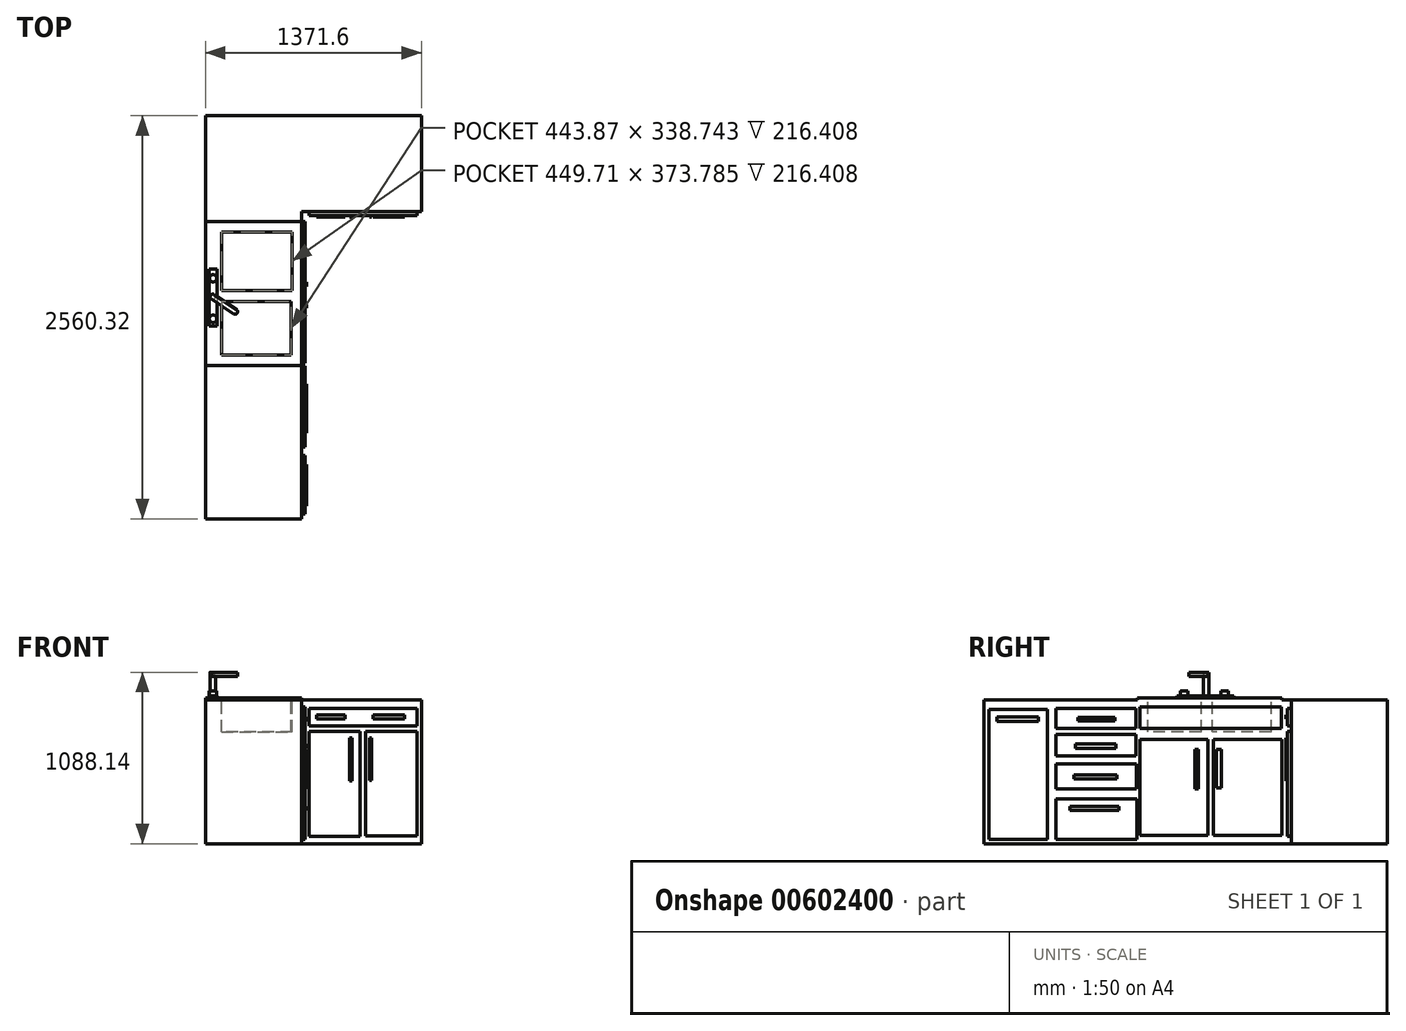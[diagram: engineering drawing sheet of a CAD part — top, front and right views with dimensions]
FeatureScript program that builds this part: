
annotation { "Feature Type Name" : "Feature", "Feature Type Description" : "" }
export const myFeature = defineFeature(function(context is Context, id is Id, definition is map)
    precondition{}
    {
        {
            var Q0;
            Q0=qCreatedBy(makeId("Top.planeOp"),FACE);
            var sketch = newSketch(context, id + "F0", { "sketchPlane" : qUnion([Q0])});
            skLineSegment(sketch, "E0", {"start": v(0, 0) * mm, "end": v(0, -2560.32) * mm});
            skLineSegment(sketch, "E1", {"start": v(0, -2560.32) * mm, "end": v(609.6, -2560.32) * mm});
            skLineSegment(sketch, "E2", {"start": v(609.6, -2560.32) * mm, "end": v(609.6, -609.6) * mm});
            skLineSegment(sketch, "E3", {"start": v(609.6, -609.6) * mm, "end": v(1371.6, -609.6) * mm});
            skLineSegment(sketch, "E4", {"start": v(1371.6, -609.6) * mm, "end": v(1371.6, 0) * mm});
            skLineSegment(sketch, "E5", {"start": v(1371.6, 0) * mm, "end": v(0, 0) * mm});
            skSolve(sketch);
        }
        {
            var Q0;
            Q0=makeQuery(id+"F0.imprint","IMPRINT",FACE,{"disambiguationData":[TD([[makeQuery(id+"F0.imprint","IMPRINT",EDGE,{"derivedFrom":sQuery(id+"F0.wireOp",EDGE,"E0")}),1.0]])]});
            extrude(context, id + "F1", {"entities" : qUnion([Q0]), "depth" : 914.4 * mm, "offsetDistance" : 30.48 * mm});
        }
        {
            var Q0;
            Q0=makeQuery(id+"F1.opExtrude","CAP_FACE",FACE,{"disambiguationData":[OSD([sQuery(id+"F0.wireOp",EDGE,"E0"),sQuery(id+"F0.wireOp",EDGE,"E1"),sQuery(id+"F0.wireOp",EDGE,"E2"),sQuery(id+"F0.wireOp",EDGE,"E3"),sQuery(id+"F0.wireOp",EDGE,"E4"),sQuery(id+"F0.wireOp",EDGE,"E5")])],"isStart":false});
            var sketch = newSketch(context, id + "F2", { "sketchPlane" : qUnion([Q0])});
            skLineSegment(sketch, "E6.bottom", {"start": v(0, -670.56) * mm, "end": v(609.6, -670.56) * mm});
            skLineSegment(sketch, "E6.top", {"start": v(0, -1584.96) * mm, "end": v(609.6, -1584.96) * mm});
            skLineSegment(sketch, "E6.left", {"start": v(0, -670.56) * mm, "end": v(0, -1584.96) * mm});
            skLineSegment(sketch, "E6.right", {"start": v(609.6, -670.56) * mm, "end": v(609.6, -1584.96) * mm});
            skSolve(sketch);
        }
        {
            var Q0;
            Q0=makeQuery(id+"F2.imprint","IMPRINT",FACE,{"disambiguationData":[TD([[makeQuery(id+"F2.imprint","IMPRINT",EDGE,{"derivedFrom":sQuery(id+"F2.wireOp",EDGE,"E6.bottom")}),-1.0]])]});
            extrude(context, id + "F3", {"entities" : qUnion([Q0]), "operationType" : NewBodyOperationType.ADD, "depth" : 12.2 * mm, "offsetDistance" : 30.48 * mm});
        }
        {
            var Q0;
            Q0=makeQuery(id+"F3.opExtrude","CAP_FACE",FACE,{"disambiguationData":[OSD([sQuery(id+"F2.wireOp",EDGE,"E6.bottom"),sQuery(id+"F2.wireOp",EDGE,"E6.top"),sQuery(id+"F2.wireOp",EDGE,"E6.left"),sQuery(id+"F2.wireOp",EDGE,"E6.right")])],"isStart":false});
            var sketch = newSketch(context, id + "F4", { "sketchPlane" : qUnion([Q0])});
            skLineSegment(sketch, "E7.bottom", {"start": v(551.33, -736.9) * mm, "end": v(101.62, -736.9) * mm});
            skLineSegment(sketch, "E7.top", {"start": v(551.33, -1110.68) * mm, "end": v(101.62, -1110.68) * mm});
            skLineSegment(sketch, "E7.left", {"start": v(551.33, -736.9) * mm, "end": v(551.33, -1110.68) * mm});
            skLineSegment(sketch, "E7.right", {"start": v(101.62, -736.9) * mm, "end": v(101.62, -1110.68) * mm});
            skLineSegment(sketch, "E8.bottom", {"start": v(101.62, -1180.77) * mm, "end": v(545.5, -1180.77) * mm});
            skLineSegment(sketch, "E8.top", {"start": v(101.62, -1519.51) * mm, "end": v(545.5, -1519.51) * mm});
            skLineSegment(sketch, "E8.left", {"start": v(101.62, -1180.77) * mm, "end": v(101.62, -1519.51) * mm});
            skLineSegment(sketch, "E8.right", {"start": v(545.5, -1180.77) * mm, "end": v(545.5, -1519.51) * mm});
            skSolve(sketch);
        }
        {
            var Q0;
            Q0=makeQuery(id+"F4.imprint","IMPRINT",FACE,{"disambiguationData":[TD([[makeQuery(id+"F4.imprint","IMPRINT",EDGE,{"derivedFrom":sQuery(id+"F4.wireOp",EDGE,"E7.bottom")}),1.0]])]});
            var Q1;
            Q1=makeQuery(id+"F4.imprint","IMPRINT",FACE,{"disambiguationData":[TD([[makeQuery(id+"F4.imprint","IMPRINT",EDGE,{"derivedFrom":sQuery(id+"F4.wireOp",EDGE,"E8.bottom")}),-1.0]])]});
            extrude(context, id + "F5", {"entities" : qUnion([Q0, Q1]), "operationType" : NewBodyOperationType.REMOVE, "oppositeDirection" : true, "depth" : 216.4 * mm, "offsetDistance" : 30.48 * mm});
        }
        {
            var Q0;
            Q0=makeQuery(id+"F3.opExtrude","CAP_FACE",FACE,{"disambiguationData":[OSD([sQuery(id+"F2.wireOp",EDGE,"E6.bottom"),sQuery(id+"F2.wireOp",EDGE,"E6.top"),sQuery(id+"F2.wireOp",EDGE,"E6.left"),sQuery(id+"F2.wireOp",EDGE,"E6.right")])],"isStart":false});
            var sketch = newSketch(context, id + "F6", { "sketchPlane" : qUnion([Q0])});
            skLineSegment(sketch, "E9.bottom", {"start": v(22.78, -973.44) * mm, "end": v(75.34, -973.44) * mm});
            skLineSegment(sketch, "E9.top", {"start": v(22.78, -1335.54) * mm, "end": v(75.34, -1335.54) * mm});
            skLineSegment(sketch, "E9.left", {"start": v(22.78, -973.44) * mm, "end": v(22.78, -1335.54) * mm});
            skLineSegment(sketch, "E9.right", {"start": v(75.34, -973.44) * mm, "end": v(75.34, -1335.54) * mm});
            skSolve(sketch);
        }
        {
            var Q0;
            Q0=makeQuery(id+"F6.imprint","IMPRINT",FACE,{"disambiguationData":[TD([[makeQuery(id+"F6.imprint","IMPRINT",EDGE,{"derivedFrom":sQuery(id+"F6.wireOp",EDGE,"E9.bottom")}),-1.0]])]});
            extrude(context, id + "F7", {"entities" : qUnion([Q0]), "operationType" : NewBodyOperationType.ADD, "depth" : 12.2 * mm, "offsetDistance" : 30.48 * mm});
        }
        {
            var Q0;
            Q0=makeQuery(id+"F7.opExtrude","CAP_FACE",FACE,{"disambiguationData":[OSD([sQuery(id+"F6.wireOp",EDGE,"E9.bottom"),sQuery(id+"F6.wireOp",EDGE,"E9.top"),sQuery(id+"F6.wireOp",EDGE,"E9.left"),sQuery(id+"F6.wireOp",EDGE,"E9.right")])],"isStart":false});
            var sketch = newSketch(context, id + "F8", { "sketchPlane" : qUnion([Q0])});
            skCircle(sketch, "E10", {"center": v(48.33, -1032.16) * mm, "radius": 23.09 * mm});
            skCircle(sketch, "E11", {"center": v(48.33, -1289.14) * mm, "radius": 23.59 * mm});
            skSolve(sketch);
        }
        {
            var Q0;
            Q0=makeQuery(id+"F8.imprint","IMPRINT",FACE,{"disambiguationData":[TD([[makeQuery(id+"F8.imprint","IMPRINT",EDGE,{"derivedFrom":sQuery(id+"F8.wireOp",EDGE,"E10")}),1.0]])]});
            var Q1;
            Q1=makeQuery(id+"F8.imprint","IMPRINT",FACE,{"disambiguationData":[TD([[makeQuery(id+"F8.imprint","IMPRINT",EDGE,{"derivedFrom":sQuery(id+"F8.wireOp",EDGE,"E11")}),1.0]])]});
            extrude(context, id + "F9", {"entities" : qUnion([Q0, Q1]), "operationType" : NewBodyOperationType.ADD, "depth" : 30.48 * mm, "offsetDistance" : 30.48 * mm});
        }
        {
            var Q0;
            Q0=makeQuery(id+"F7.opExtrude","CAP_FACE",FACE,{"disambiguationData":[OSD([sQuery(id+"F6.wireOp",EDGE,"E9.bottom"),sQuery(id+"F6.wireOp",EDGE,"E9.top"),sQuery(id+"F6.wireOp",EDGE,"E9.left"),sQuery(id+"F6.wireOp",EDGE,"E9.right")])],"isStart":false});
            var sketch = newSketch(context, id + "F10", { "sketchPlane" : qUnion([Q0])});
            skCircle(sketch, "E12", {"center": v(46.5, -1150.24) * mm, "radius": 16.93 * mm});
            skSolve(sketch);
        }
        {
            var Q0;
            Q0=makeQuery(id+"F10.imprint","IMPRINT",FACE,{"disambiguationData":[TD([[makeQuery(id+"F10.imprint","IMPRINT",EDGE,{"derivedFrom":sQuery(id+"F10.wireOp",EDGE,"E12")}),1.0]])]});
            extrude(context, id + "F11", {"entities" : qUnion([Q0]), "operationType" : NewBodyOperationType.ADD, "depth" : 149.35 * mm, "offsetDistance" : 30.48 * mm});
        }
        {
            var Q0;
            Q0=makeQuery(id+"F11.opExtrude","CAP_FACE",FACE,{"disambiguationData":[OSD([sQuery(id+"F10.wireOp",EDGE,"E12")])],"isStart":false});
            var sketch = newSketch(context, id + "F12", { "sketchPlane" : qUnion([Q0])});
            skCircle(sketch, "E13", {"center": v(188.51, -1244.37) * mm, "radius": 15.96 * mm});
            skLineSegment(sketch, "E14", {"start": v(50.89, -1133.88) * mm, "end": v(197.34, -1231.08) * mm});
            skLineSegment(sketch, "E15", {"start": v(36.16, -1163.65) * mm, "end": v(179.77, -1257.73) * mm});
            skSolve(sketch);
        }
        {
            var Q0;
            {var subQ0=sQuery(id+"F12.wireOp",EDGE,"E14");var subQ1=sQuery(id+"F12.wireOp",EDGE,"E13");var subQ2=makeQuery(id+"F12.imprint","INTERSECT",VERTEX,{"derivedFrom":[subQ1,subQ0]});Q0=makeQuery(id+"F12.imprint","IMPRINT",FACE,{"disambiguationData":[TD([[makeQuery(id+"F12.imprint","IMPRINT",EDGE,{"disambiguationData":[TD([[subQ2,-1.0]])],"derivedFrom":subQ1}),-1.0]])]});}
            var Q1;
            {var subQ0=sQuery(id+"F12.wireOp",EDGE,"E13");var subQ1=makeQuery(id+"F12.imprint","INTERSECT",VERTEX,{"derivedFrom":[subQ0,sQuery(id+"F12.wireOp",EDGE,"E14")]});Q1=makeQuery(id+"F12.imprint","IMPRINT",FACE,{"disambiguationData":[TD([[makeQuery(id+"F12.imprint","IMPRINT",EDGE,{"disambiguationData":[TD([[subQ1,-1.0]])],"derivedFrom":subQ0}),1.0]])]});}
            extrude(context, id + "F13", {"entities" : qUnion([Q0, Q1]), "operationType" : NewBodyOperationType.ADD, "oppositeDirection" : true, "depth" : 26.21 * mm, "offsetDistance" : 30.48 * mm});
        }
        {
            var Q0;
            Q0=makeQuery(id+"F3.boolean.opBoolean","MERGE",FACE,{"derivedFrom":[makeQuery(id+"F1.opExtrude","SWEPT_FACE",FACE,{"disambiguationData":[OSD([sQuery(id+"F0.wireOp",EDGE,"E2")])]}),makeQuery(id+"F3.opExtrude","SWEPT_FACE",FACE,{"disambiguationData":[OSD([sQuery(id+"F2.wireOp",EDGE,"E6.right")])]})]});
            var sketch = newSketch(context, id + "F14", { "sketchPlane" : qUnion([Q0])});
            skLineSegment(sketch, "E16.bottom", {"start": v(-2529.26, 852.66) * mm, "end": v(-2157.31, 852.66) * mm});
            skLineSegment(sketch, "E16.top", {"start": v(-2529.26, 26.4) * mm, "end": v(-2157.31, 26.4) * mm});
            skLineSegment(sketch, "E16.left", {"start": v(-2529.26, 852.66) * mm, "end": v(-2529.26, 26.4) * mm});
            skLineSegment(sketch, "E16.right", {"start": v(-2157.31, 852.66) * mm, "end": v(-2157.31, 26.4) * mm});
            skLineSegment(sketch, "E17.bottom", {"start": v(-2104.18, 857.97) * mm, "end": v(-1596.74, 857.97) * mm});
            skLineSegment(sketch, "E17.top", {"start": v(-2104.18, 733.1) * mm, "end": v(-1596.74, 733.1) * mm});
            skLineSegment(sketch, "E17.left", {"start": v(-2104.18, 857.97) * mm, "end": v(-2104.18, 733.1) * mm});
            skLineSegment(sketch, "E17.right", {"start": v(-1596.74, 857.97) * mm, "end": v(-1596.74, 733.1) * mm});
            skLineSegment(sketch, "E18.bottom", {"start": v(-2104.18, 693.25) * mm, "end": v(-1596.74, 693.25) * mm});
            skLineSegment(sketch, "E18.top", {"start": v(-2104.18, 557.76) * mm, "end": v(-1596.74, 557.76) * mm});
            skLineSegment(sketch, "E18.left", {"start": v(-2104.18, 693.25) * mm, "end": v(-2104.18, 557.76) * mm});
            skLineSegment(sketch, "E18.right", {"start": v(-1596.74, 693.25) * mm, "end": v(-1596.74, 557.76) * mm});
            skLineSegment(sketch, "E19.bottom", {"start": v(-2104.18, 507.28) * mm, "end": v(-1594.08, 507.28) * mm});
            skLineSegment(sketch, "E19.top", {"start": v(-2104.18, 347.88) * mm, "end": v(-1594.08, 347.88) * mm});
            skLineSegment(sketch, "E19.left", {"start": v(-2104.18, 507.28) * mm, "end": v(-2104.18, 347.88) * mm});
            skLineSegment(sketch, "E19.right", {"start": v(-1594.08, 507.28) * mm, "end": v(-1594.08, 347.88) * mm});
            skLineSegment(sketch, "E20.bottom", {"start": v(-2104.18, 284.11) * mm, "end": v(-1588.77, 284.11) * mm});
            skLineSegment(sketch, "E20.top", {"start": v(-2104.18, 26.4) * mm, "end": v(-1588.77, 26.4) * mm});
            skLineSegment(sketch, "E20.left", {"start": v(-2104.18, 284.11) * mm, "end": v(-2104.18, 26.4) * mm});
            skLineSegment(sketch, "E20.right", {"start": v(-1588.77, 284.11) * mm, "end": v(-1588.77, 26.4) * mm});
            skLineSegment(sketch, "E21.bottom", {"start": v(-1570.17, 868.6) * mm, "end": v(-672.18, 868.6) * mm});
            skLineSegment(sketch, "E21.top", {"start": v(-1570.17, 733.1) * mm, "end": v(-672.18, 733.1) * mm});
            skLineSegment(sketch, "E21.left", {"start": v(-1570.17, 868.6) * mm, "end": v(-1570.17, 733.1) * mm});
            skLineSegment(sketch, "E21.right", {"start": v(-672.18, 868.6) * mm, "end": v(-672.18, 733.1) * mm});
            skLineSegment(sketch, "E22.bottom", {"start": v(-1570.17, 661.37) * mm, "end": v(-1139.77, 661.37) * mm});
            skLineSegment(sketch, "E22.top", {"start": v(-1570.17, 52.97) * mm, "end": v(-1139.77, 52.97) * mm});
            skLineSegment(sketch, "E22.left", {"start": v(-1570.17, 661.37) * mm, "end": v(-1570.17, 52.97) * mm});
            skLineSegment(sketch, "E22.right", {"start": v(-1139.77, 661.37) * mm, "end": v(-1139.77, 52.97) * mm});
            skLineSegment(sketch, "E23.bottom", {"start": v(-1105.24, 661.37) * mm, "end": v(-670.56, 661.37) * mm});
            skLineSegment(sketch, "E23.top", {"start": v(-1105.24, 52.97) * mm, "end": v(-670.56, 52.97) * mm});
            skLineSegment(sketch, "E23.left", {"start": v(-1105.24, 661.37) * mm, "end": v(-1105.24, 52.97) * mm});
            skLineSegment(sketch, "E23.right", {"start": v(-670.56, 661.37) * mm, "end": v(-670.56, 52.97) * mm});
            skSolve(sketch);
        }
        {
            var Q0;
            Q0=makeQuery(id+"F14.imprint","IMPRINT",FACE,{"disambiguationData":[TD([[makeQuery(id+"F14.imprint","IMPRINT",EDGE,{"derivedFrom":sQuery(id+"F14.wireOp",EDGE,"E21.bottom")}),-1.0]])]});
            var Q1;
            Q1=makeQuery(id+"F14.imprint","IMPRINT",FACE,{"disambiguationData":[TD([[makeQuery(id+"F14.imprint","IMPRINT",EDGE,{"derivedFrom":sQuery(id+"F14.wireOp",EDGE,"E22.bottom")}),-1.0]])]});
            var Q2;
            Q2=makeQuery(id+"F14.imprint","IMPRINT",FACE,{"disambiguationData":[TD([[makeQuery(id+"F14.imprint","IMPRINT",EDGE,{"derivedFrom":sQuery(id+"F14.wireOp",EDGE,"E23.bottom")}),-1.0]])]});
            var Q3;
            Q3=makeQuery(id+"F14.imprint","IMPRINT",FACE,{"disambiguationData":[TD([[makeQuery(id+"F14.imprint","IMPRINT",EDGE,{"derivedFrom":sQuery(id+"F14.wireOp",EDGE,"E17.bottom")}),-1.0]])]});
            var Q4;
            Q4=makeQuery(id+"F14.imprint","IMPRINT",FACE,{"disambiguationData":[TD([[makeQuery(id+"F14.imprint","IMPRINT",EDGE,{"derivedFrom":sQuery(id+"F14.wireOp",EDGE,"E18.bottom")}),-1.0]])]});
            var Q5;
            Q5=makeQuery(id+"F14.imprint","IMPRINT",FACE,{"disambiguationData":[TD([[makeQuery(id+"F14.imprint","IMPRINT",EDGE,{"derivedFrom":sQuery(id+"F14.wireOp",EDGE,"E19.bottom")}),-1.0]])]});
            var Q6;
            Q6=makeQuery(id+"F14.imprint","IMPRINT",FACE,{"disambiguationData":[TD([[makeQuery(id+"F14.imprint","IMPRINT",EDGE,{"derivedFrom":sQuery(id+"F14.wireOp",EDGE,"E20.bottom")}),-1.0]])]});
            var Q7;
            Q7=makeQuery(id+"F14.imprint","IMPRINT",FACE,{"disambiguationData":[TD([[makeQuery(id+"F14.imprint","IMPRINT",EDGE,{"derivedFrom":sQuery(id+"F14.wireOp",EDGE,"E16.bottom")}),-1.0]])]});
            extrude(context, id + "F15", {"entities" : qUnion([Q0, Q1, Q2, Q3, Q4, Q5, Q6, Q7]), "operationType" : NewBodyOperationType.ADD, "depth" : 24.38 * mm, "offsetDistance" : 30.48 * mm});
        }
        {
            var Q0;
            Q0=makeQuery(id+"F3.boolean.opBoolean","MERGE",FACE,{"derivedFrom":[makeQuery(id+"F1.opExtrude","SWEPT_FACE",FACE,{"disambiguationData":[OSD([sQuery(id+"F0.wireOp",EDGE,"E2")])]}),makeQuery(id+"F3.opExtrude","SWEPT_FACE",FACE,{"disambiguationData":[OSD([sQuery(id+"F2.wireOp",EDGE,"E6.right")])]})]});
            var sketch = newSketch(context, id + "F16", { "sketchPlane" : qUnion([Q0])});
            skLineSegment(sketch, "E24.bottom", {"start": v(-2478.78, 804.84) * mm, "end": v(-2215.76, 804.84) * mm});
            skLineSegment(sketch, "E24.top", {"start": v(-2478.78, 775.61) * mm, "end": v(-2215.76, 775.61) * mm});
            skLineSegment(sketch, "E24.left", {"start": v(-2478.78, 804.84) * mm, "end": v(-2478.78, 775.61) * mm});
            skLineSegment(sketch, "E24.right", {"start": v(-2215.76, 804.84) * mm, "end": v(-2215.76, 775.61) * mm});
            skLineSegment(sketch, "E25.bottom", {"start": v(-1966.03, 802.18) * mm, "end": v(-1729.58, 802.18) * mm});
            skLineSegment(sketch, "E25.top", {"start": v(-1966.03, 780.93) * mm, "end": v(-1729.58, 780.93) * mm});
            skLineSegment(sketch, "E25.left", {"start": v(-1966.03, 802.18) * mm, "end": v(-1966.03, 780.93) * mm});
            skLineSegment(sketch, "E25.right", {"start": v(-1729.58, 802.18) * mm, "end": v(-1729.58, 780.93) * mm});
            skLineSegment(sketch, "E26.bottom", {"start": v(-1979.31, 634.8) * mm, "end": v(-1721.6, 634.8) * mm});
            skLineSegment(sketch, "E26.top", {"start": v(-1979.31, 605.58) * mm, "end": v(-1721.6, 605.58) * mm});
            skLineSegment(sketch, "E26.left", {"start": v(-1979.31, 634.8) * mm, "end": v(-1979.31, 605.58) * mm});
            skLineSegment(sketch, "E26.right", {"start": v(-1721.6, 634.8) * mm, "end": v(-1721.6, 605.58) * mm});
            skLineSegment(sketch, "E27.bottom", {"start": v(-1989.94, 438.2) * mm, "end": v(-1716.3, 438.2) * mm});
            skLineSegment(sketch, "E27.top", {"start": v(-1989.94, 411.64) * mm, "end": v(-1716.3, 411.64) * mm});
            skLineSegment(sketch, "E27.left", {"start": v(-1989.94, 438.2) * mm, "end": v(-1989.94, 411.64) * mm});
            skLineSegment(sketch, "E27.right", {"start": v(-1716.3, 438.2) * mm, "end": v(-1716.3, 411.64) * mm});
            skLineSegment(sketch, "E28.bottom", {"start": v(-2013.85, 236.3) * mm, "end": v(-1703, 236.3) * mm});
            skLineSegment(sketch, "E28.top", {"start": v(-2013.85, 212.38) * mm, "end": v(-1703, 212.38) * mm});
            skLineSegment(sketch, "E28.left", {"start": v(-2013.85, 236.3) * mm, "end": v(-2013.85, 212.38) * mm});
            skLineSegment(sketch, "E28.right", {"start": v(-1703, 236.3) * mm, "end": v(-1703, 212.38) * mm});
            skLineSegment(sketch, "E29.bottom", {"start": v(-1222.13, 597.61) * mm, "end": v(-1198.22, 597.61) * mm});
            skLineSegment(sketch, "E29.top", {"start": v(-1222.13, 347.88) * mm, "end": v(-1198.22, 347.88) * mm});
            skLineSegment(sketch, "E29.left", {"start": v(-1222.13, 597.61) * mm, "end": v(-1222.13, 347.88) * mm});
            skLineSegment(sketch, "E29.right", {"start": v(-1198.22, 597.61) * mm, "end": v(-1198.22, 347.88) * mm});
            skLineSegment(sketch, "E30.bottom", {"start": v(-1083.98, 597.61) * mm, "end": v(-1054.76, 597.61) * mm});
            skLineSegment(sketch, "E30.top", {"start": v(-1083.98, 353.19) * mm, "end": v(-1054.76, 353.19) * mm});
            skLineSegment(sketch, "E30.left", {"start": v(-1083.98, 597.61) * mm, "end": v(-1083.98, 353.19) * mm});
            skLineSegment(sketch, "E30.right", {"start": v(-1054.76, 597.61) * mm, "end": v(-1054.76, 353.19) * mm});
            skSolve(sketch);
        }
        {
            var Q0;
            Q0 = qSketchRegion(id + "F16", true);
            extrude(context, id + "F17", {"entities" : qUnion([Q0]), "operationType" : NewBodyOperationType.ADD, "depth" : 33.53 * mm, "offsetDistance" : 30.48 * mm});
        }
        {
            var Q0;
            Q0=makeQuery(id+"F1.opExtrude","SWEPT_FACE",FACE,{"disambiguationData":[OSD([sQuery(id+"F0.wireOp",EDGE,"E3")])]});
            var sketch = newSketch(context, id + "F18", { "sketchPlane" : qUnion([Q0])});
            skLineSegment(sketch, "E31.bottom", {"start": v(656.73, 858.02) * mm, "end": v(1342.8, 858.02) * mm});
            skLineSegment(sketch, "E31.top", {"start": v(656.73, 749.7) * mm, "end": v(1342.8, 749.7) * mm});
            skLineSegment(sketch, "E31.left", {"start": v(656.73, 858.02) * mm, "end": v(656.73, 749.7) * mm});
            skLineSegment(sketch, "E31.right", {"start": v(1342.8, 858.02) * mm, "end": v(1342.8, 749.7) * mm});
            skLineSegment(sketch, "E32.bottom", {"start": v(656.73, 713.58) * mm, "end": v(981.7, 713.58) * mm});
            skLineSegment(sketch, "E32.top", {"start": v(656.73, 45.56) * mm, "end": v(981.7, 45.56) * mm});
            skLineSegment(sketch, "E32.left", {"start": v(656.73, 713.58) * mm, "end": v(656.73, 45.56) * mm});
            skLineSegment(sketch, "E32.right", {"start": v(981.7, 713.58) * mm, "end": v(981.7, 45.56) * mm});
            skLineSegment(sketch, "E33.bottom", {"start": v(1342.8, 713.58) * mm, "end": v(1017.82, 713.58) * mm});
            skLineSegment(sketch, "E33.top", {"start": v(1342.8, 48.14) * mm, "end": v(1017.82, 48.14) * mm});
            skLineSegment(sketch, "E33.left", {"start": v(1342.8, 713.58) * mm, "end": v(1342.8, 48.14) * mm});
            skLineSegment(sketch, "E33.right", {"start": v(1017.82, 713.58) * mm, "end": v(1017.82, 48.14) * mm});
            skSolve(sketch);
        }
        {
            var Q0;
            Q0=makeQuery(id+"F18.imprint","IMPRINT",FACE,{"disambiguationData":[TD([[makeQuery(id+"F18.imprint","IMPRINT",EDGE,{"derivedFrom":sQuery(id+"F18.wireOp",EDGE,"E31.bottom")}),-1.0]])]});
            var Q1;
            Q1=makeQuery(id+"F18.imprint","IMPRINT",FACE,{"disambiguationData":[TD([[makeQuery(id+"F18.imprint","IMPRINT",EDGE,{"derivedFrom":sQuery(id+"F18.wireOp",EDGE,"E32.bottom")}),-1.0]])]});
            var Q2;
            Q2=makeQuery(id+"F18.imprint","IMPRINT",FACE,{"disambiguationData":[TD([[makeQuery(id+"F18.imprint","IMPRINT",EDGE,{"derivedFrom":sQuery(id+"F18.wireOp",EDGE,"E33.bottom")}),1.0]])]});
            extrude(context, id + "F19", {"entities" : qUnion([Q0, Q1, Q2]), "operationType" : NewBodyOperationType.ADD, "depth" : 24.38 * mm, "offsetDistance" : 30.48 * mm});
        }
        {
            var Q0;
            Q0=makeQuery(id+"F1.opExtrude","SWEPT_FACE",FACE,{"disambiguationData":[OSD([sQuery(id+"F0.wireOp",EDGE,"E3")])]});
            var sketch = newSketch(context, id + "F20", { "sketchPlane" : qUnion([Q0])});
            skLineSegment(sketch, "E34.bottom", {"start": v(705.73, 819.33) * mm, "end": v(886.28, 819.33) * mm});
            skLineSegment(sketch, "E34.top", {"start": v(705.73, 793.54) * mm, "end": v(886.28, 793.54) * mm});
            skLineSegment(sketch, "E34.left", {"start": v(705.73, 819.33) * mm, "end": v(705.73, 793.54) * mm});
            skLineSegment(sketch, "E34.right", {"start": v(886.28, 819.33) * mm, "end": v(886.28, 793.54) * mm});
            skLineSegment(sketch, "E35.bottom", {"start": v(1064.24, 819.33) * mm, "end": v(1265.42, 819.33) * mm});
            skLineSegment(sketch, "E35.top", {"start": v(1064.24, 793.54) * mm, "end": v(1265.42, 793.54) * mm});
            skLineSegment(sketch, "E35.left", {"start": v(1064.24, 819.33) * mm, "end": v(1064.24, 793.54) * mm});
            skLineSegment(sketch, "E35.right", {"start": v(1265.42, 819.33) * mm, "end": v(1265.42, 793.54) * mm});
            skLineSegment(sketch, "E36.bottom", {"start": v(914.65, 672.31) * mm, "end": v(932.7, 672.31) * mm});
            skLineSegment(sketch, "E36.top", {"start": v(914.65, 398.92) * mm, "end": v(932.7, 398.92) * mm});
            skLineSegment(sketch, "E36.left", {"start": v(914.65, 672.31) * mm, "end": v(914.65, 398.92) * mm});
            skLineSegment(sketch, "E36.right", {"start": v(932.7, 672.31) * mm, "end": v(932.7, 398.92) * mm});
            skLineSegment(sketch, "E37.bottom", {"start": v(1041.03, 672.31) * mm, "end": v(1056.5, 672.31) * mm});
            skLineSegment(sketch, "E37.top", {"start": v(1041.03, 401.5) * mm, "end": v(1056.5, 401.5) * mm});
            skLineSegment(sketch, "E37.left", {"start": v(1041.03, 672.31) * mm, "end": v(1041.03, 401.5) * mm});
            skLineSegment(sketch, "E37.right", {"start": v(1056.5, 672.31) * mm, "end": v(1056.5, 401.5) * mm});
            skSolve(sketch);
        }
        {
            var Q0;
            Q0 = qSketchRegion(id + "F20", true);
            extrude(context, id + "F21", {"entities" : qUnion([Q0]), "operationType" : NewBodyOperationType.ADD, "depth" : 33.53 * mm, "offsetDistance" : 30.48 * mm});
        }
    });
